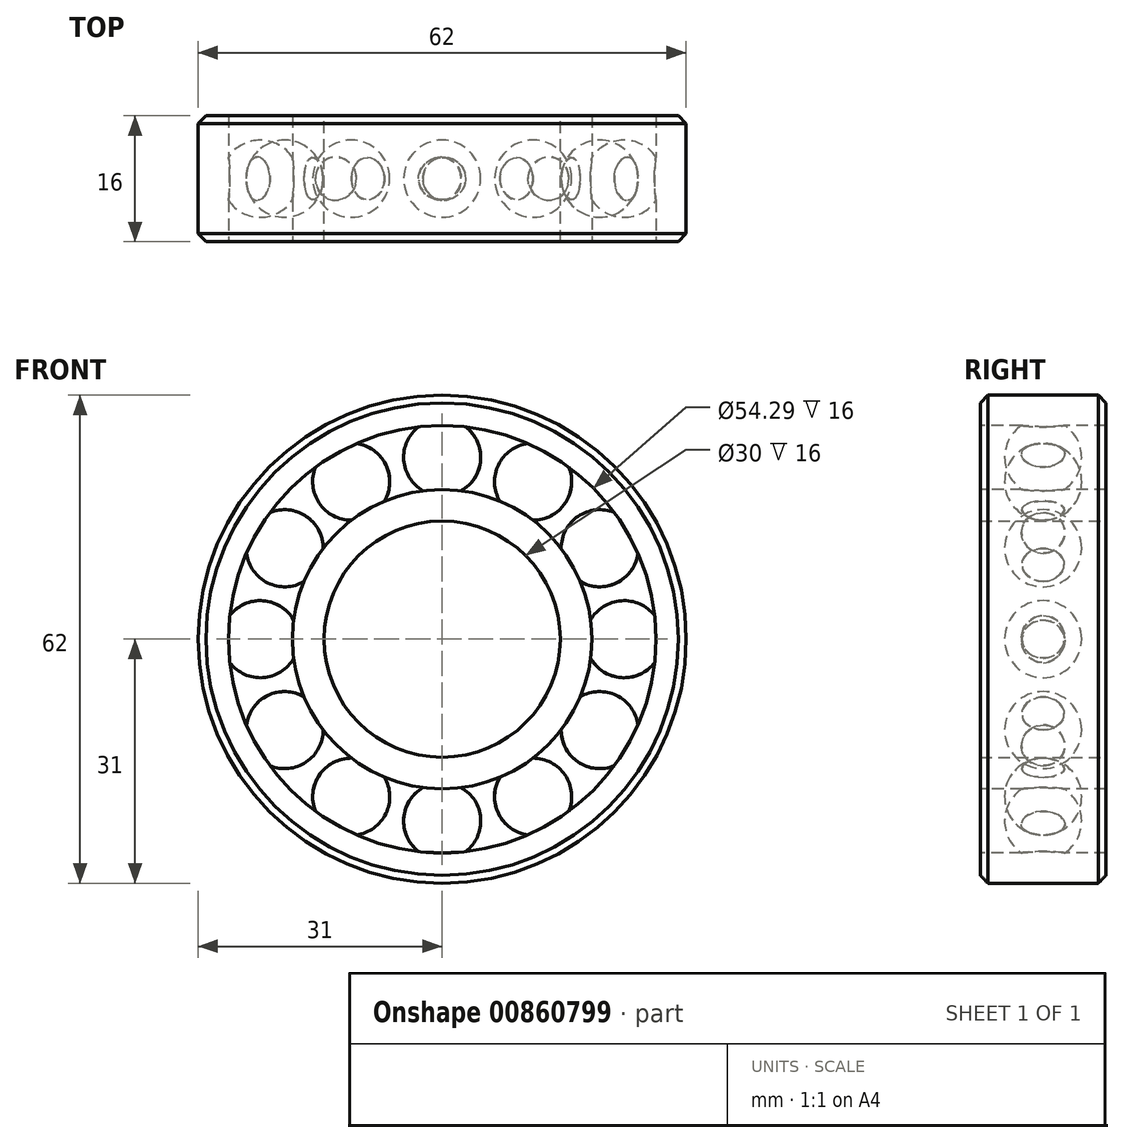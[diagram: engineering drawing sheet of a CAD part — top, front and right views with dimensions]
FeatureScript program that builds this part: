
annotation { "Feature Type Name" : "Feature", "Feature Type Description" : "" }
export const myFeature = defineFeature(function(context is Context, id is Id, definition is map)
    precondition{}
    {
        {
            var Q0;
            Q0=qCreatedBy(makeId("Front.planeOp"),FACE);
            var sketch = newSketch(context, id + "F0", { "sketchPlane" : qUnion([Q0])});
            skCircle(sketch, "E0", {"center": v(0, 0) * mm, "radius": 31 * mm});
            skCircle(sketch, "E1", {"center": v(0, 0) * mm, "radius": 15 * mm});
            skSolve(sketch);
        }
        {
            var Q0;
            Q0 = qSketchRegion(id + "F0", true);
            extrude(context, id + "F1", {"entities" : qUnion([Q0]), "endBound" : BoundingType.SYMMETRIC, "depth" : 16 * mm, "offsetDistance" : 25 * mm});
        }
        {
            var Q0;
            Q0=makeQuery(id+"F1.opExtrude","CAP_FACE",FACE,{"disambiguationData":[OSD([sQuery(id+"F0.wireOp",EDGE,"E0"),sQuery(id+"F0.wireOp",EDGE,"E1")])],"isStart":false});
            var sketch = newSketch(context, id + "F2", { "sketchPlane" : qUnion([Q0])});
            skCircle(sketch, "E2", {"center": v(0, 0) * mm, "radius": 27.14 * mm});
            skCircle(sketch, "E3", {"center": v(0, 0) * mm, "radius": 19 * mm});
            skSolve(sketch);
        }
        {
            var Q0;
            Q0 = qSketchRegion(id + "F2", true);
            extrude(context, id + "F3", {"entities" : qUnion([Q0]), "operationType" : NewBodyOperationType.REMOVE, "oppositeDirection" : true, "depth" : 25 * mm, "offsetDistance" : 25 * mm});
        }
        {
            var Q0;
            Q0=qCreatedBy(makeId("Front.planeOp"),FACE);
            var sketch = newSketch(context, id + "F4", { "sketchPlane" : qUnion([Q0])});
            skArc(sketch, "E4", {"start": v(0, 28) * mm, "mid": v(-4.9, 23.1) * mm, "end": v(0, 18.21) * mm});
            skLineSegment(sketch, "E5", {"start": v(0, 28) * mm, "end": v(0, 18.21) * mm});
            skSolve(sketch);
        }
        {
            var Q0;
            Q0 = qSketchRegion(id + "F4", true);
            var Q1;
            Q1=sQuery(id+"F4.wireOp",EDGE,"E5");
            revolve(context, id + "F5", {"operationType" : NewBodyOperationType.ADD, "surfaceOperationType" : NewSurfaceOperationType.NEW, "entities" : qUnion([Q0]), "axis" : qUnion([Q1]), "revolveType" : RevolveType.FULL});
        }
        {
            var Q0;
            Q0=makeQuery(id+"F3.boolean.opBoolean","SPLIT",BODY,{"disambiguationData":[OD(0.0)],"derivedFrom":makeQuery(id+"F1.opExtrude","SWEPT_BODY",BODY,{"disambiguationData":[OSD([sQuery(id+"F0.wireOp",EDGE,"E0"),sQuery(id+"F0.wireOp",EDGE,"E1")])]})});
            var Q1;
            Q1=makeQuery(id+"F1.opExtrude","SWEPT_FACE",FACE,{"disambiguationData":[OSD([sQuery(id+"F0.wireOp",EDGE,"E1")])]});
            circularPattern(context, id + "F6", {"operationType" : NewBodyOperationType.ADD, "entities" : qUnion([Q0]), "axis" : qUnion([Q1]), "angle" : 360 * degree, "instanceCount" : 12, "equalSpace" : true});
        }
        {
            var Q0;
            Q0=makeQuery(id+"F1.opExtrude","CAP_EDGE",EDGE,{"disambiguationData":[OSD([sQuery(id+"F0.wireOp",EDGE,"E0")])],"isStart":false});
            var Q1;
            Q1=makeQuery(id+"F1.opExtrude","CAP_EDGE",EDGE,{"disambiguationData":[OSD([sQuery(id+"F0.wireOp",EDGE,"E0")])],"isStart":true});
            chamfer(context, id + "F7", {"entities" : qUnion([Q0, Q1]), "width" : 1 * mm, "tangentPropagation" : true});
        }
    });
